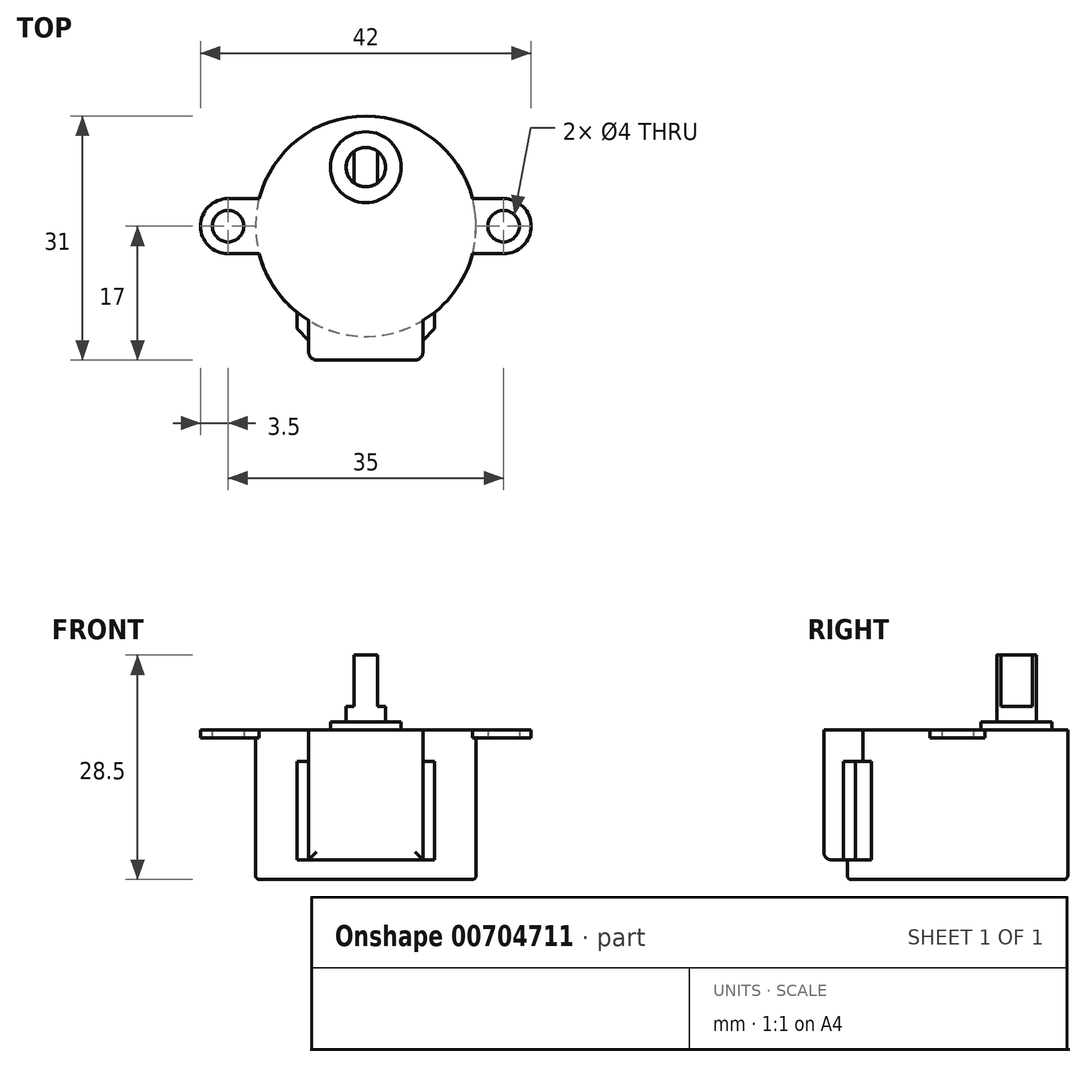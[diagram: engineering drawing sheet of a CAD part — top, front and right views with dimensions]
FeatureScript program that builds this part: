
annotation { "Feature Type Name" : "Feature", "Feature Type Description" : "" }
export const myFeature = defineFeature(function(context is Context, id is Id, definition is map)
    precondition{}
    {
        {
            var Q0;
            Q0=qCreatedBy(makeId("Top.planeOp"),FACE);
            var sketch = newSketch(context, id + "F0", { "sketchPlane" : qUnion([Q0])});
            skCircle(sketch, "E0", {"center": v(0, 0) * mm, "radius": 2.5 * mm});
            skLineSegment(sketch, "E1.bottom", {"start": v(-1.5, 2.88) * mm, "end": v(1.5, 2.88) * mm});
            skLineSegment(sketch, "E1.top", {"start": v(-1.5, -3.12) * mm, "end": v(1.5, -3.12) * mm});
            skLineSegment(sketch, "E1.left", {"start": v(-1.5, 2.88) * mm, "end": v(-1.5, -3.12) * mm});
            skLineSegment(sketch, "E1.right", {"start": v(1.5, 2.88) * mm, "end": v(1.5, -3.12) * mm});
            skCircle(sketch, "E2", {"center": v(0, 0) * mm, "radius": 4.5 * mm});
            skCircle(sketch, "E3", {"center": v(0, -7.5) * mm, "radius": 14 * mm});
            skCircle(sketch, "E4", {"center": v(17.5, -7.5) * mm, "radius": 2 * mm});
            skCircle(sketch, "E5", {"center": v(-17.5, -7.5) * mm, "radius": 2 * mm});
            skLineSegment(sketch, "E6", {"start": v(-37.47, -7.5) * mm, "end": v(35.56, -7.5) * mm, "construction": true});
            skCircle(sketch, "E7", {"center": v(17.5, -7.5) * mm, "radius": 3.5 * mm});
            skCircle(sketch, "E8", {"center": v(-17.5, -7.5) * mm, "radius": 3.5 * mm});
            skLineSegment(sketch, "E9", {"start": v(-17.5, -4) * mm, "end": v(17.5, -4) * mm});
            skLineSegment(sketch, "E10", {"start": v(-17.5, -11) * mm, "end": v(17.5, -11) * mm});
            skLineSegment(sketch, "E11.bottom", {"start": v(-7.25, -19.5) * mm, "end": v(7.25, -19.5) * mm});
            skLineSegment(sketch, "E11.top", {"start": v(-7.25, -24.5) * mm, "end": v(7.25, -24.5) * mm});
            skLineSegment(sketch, "E11.left", {"start": v(-7.25, -19.5) * mm, "end": v(-7.25, -24.5) * mm});
            skLineSegment(sketch, "E11.right", {"start": v(7.25, -19.5) * mm, "end": v(7.25, -24.5) * mm});
            skLineSegment(sketch, "E12.bottom", {"start": v(-8.75, -12.5) * mm, "end": v(8.75, -12.5) * mm});
            skLineSegment(sketch, "E12.top", {"start": v(-8.75, -20.5) * mm, "end": v(8.75, -20.5) * mm});
            skLineSegment(sketch, "E12.left", {"start": v(-8.75, -12.5) * mm, "end": v(-8.75, -20.5) * mm});
            skLineSegment(sketch, "E12.right", {"start": v(8.75, -12.5) * mm, "end": v(8.75, -20.5) * mm});
            skLineSegment(sketch, "E13", {"start": v(8.75, -20.5) * mm, "end": v(7.25, -22) * mm});
            skLineSegment(sketch, "E14", {"start": v(-8.75, -20.5) * mm, "end": v(-7.25, -22) * mm});
            skSolve(sketch);
        }
        {
            var Q0;
            {var subQ0=sQuery(id+"F0.wireOp",EDGE,"E9");var subQ9=sQuery(id+"F0.wireOp",EDGE,"E2");var subQ10=makeQuery(id+"F0.imprint","INTERSECT",VERTEX,{"disambiguationData":[OD(0.0)],"derivedFrom":[subQ9,subQ0]});Q0=makeQuery(id+"F0.imprint","IMPRINT",FACE,{"disambiguationData":[TD([[makeQuery(id+"F0.imprint","IMPRINT",EDGE,{"disambiguationData":[TD([[subQ10,-1.0]])],"derivedFrom":subQ9}),-1.0]])]});}
            var Q1;
            Q1=makeQuery(id+"F0.imprint","IMPRINT",FACE,{"disambiguationData":[TD([[makeQuery(id+"F0.imprint","IMPRINT",EDGE,{"derivedFrom":sQuery(id+"F0.wireOp",EDGE,"E4")}),-1.0]])]});
            var Q2;
            Q2=makeQuery(id+"F0.imprint","IMPRINT",FACE,{"disambiguationData":[TD([[makeQuery(id+"F0.imprint","IMPRINT",EDGE,{"derivedFrom":sQuery(id+"F0.wireOp",EDGE,"E5")}),-1.0]])]});
            var Q3;
            {var subQ0=sQuery(id+"F0.wireOp",EDGE,"E9");var subQ1=sQuery(id+"F0.wireOp",EDGE,"E3");var subQ2=makeQuery(id+"F0.imprint","INTERSECT",VERTEX,{"disambiguationData":[OD(1.0)],"derivedFrom":[subQ1,subQ0]});Q3=makeQuery(id+"F0.imprint","IMPRINT",FACE,{"disambiguationData":[TD([[makeQuery(id+"F0.imprint","IMPRINT",EDGE,{"disambiguationData":[TD([[subQ2,-1.0]])],"derivedFrom":subQ1}),-1.0]])]});}
            var Q4;
            {var subQ0=sQuery(id+"F0.wireOp",EDGE,"E10");var subQ1=sQuery(id+"F0.wireOp",EDGE,"E3");var subQ2=makeQuery(id+"F0.imprint","INTERSECT",VERTEX,{"disambiguationData":[OD(0.0)],"derivedFrom":[subQ1,subQ0]});Q4=makeQuery(id+"F0.imprint","IMPRINT",FACE,{"disambiguationData":[TD([[makeQuery(id+"F0.imprint","IMPRINT",EDGE,{"disambiguationData":[TD([[subQ2,1.0]])],"derivedFrom":subQ1}),-1.0]])]});}
            var Q5;
            {var subQ0=sQuery(id+"F0.wireOp",EDGE,"E12.bottom");Q5=makeQuery(id+"F0.imprint","IMPRINT",FACE,{"disambiguationData":[TD([[makeQuery(id+"F0.imprint","IMPRINT",EDGE,{"derivedFrom":subQ0}),1.0]])]});}
            var Q6;
            {var subQ0=sQuery(id+"F0.wireOp",EDGE,"E12.bottom");Q6=makeQuery(id+"F0.imprint","IMPRINT",FACE,{"disambiguationData":[TD([[makeQuery(id+"F0.imprint","IMPRINT",EDGE,{"derivedFrom":subQ0}),-1.0]])]});}
            var Q7;
            {var subQ0=sQuery(id+"F0.wireOp",EDGE,"E9");var subQ1=sQuery(id+"F0.wireOp",EDGE,"E2");var subQ2=makeQuery(id+"F0.imprint","INTERSECT",VERTEX,{"disambiguationData":[OD(0.0)],"derivedFrom":[subQ1,subQ0]});Q7=makeQuery(id+"F0.imprint","IMPRINT",FACE,{"disambiguationData":[TD([[makeQuery(id+"F0.imprint","IMPRINT",EDGE,{"disambiguationData":[TD([[subQ2,1.0]])],"derivedFrom":subQ1}),-1.0]])]});}
            var Q8;
            {var subQ0=sQuery(id+"F0.wireOp",EDGE,"E9");var subQ1=sQuery(id+"F0.wireOp",EDGE,"E3");var subQ2=makeQuery(id+"F0.imprint","INTERSECT",VERTEX,{"disambiguationData":[OD(0.0)],"derivedFrom":[subQ1,subQ0]});Q8=makeQuery(id+"F0.imprint","IMPRINT",FACE,{"disambiguationData":[TD([[makeQuery(id+"F0.imprint","IMPRINT",EDGE,{"disambiguationData":[TD([[subQ2,1.0]])],"derivedFrom":subQ1}),-1.0]])]});}
            var Q9;
            {var subQ0=sQuery(id+"F0.wireOp",EDGE,"E10");var subQ1=sQuery(id+"F0.wireOp",EDGE,"E3");var subQ2=makeQuery(id+"F0.imprint","INTERSECT",VERTEX,{"disambiguationData":[OD(1.0)],"derivedFrom":[subQ1,subQ0]});Q9=makeQuery(id+"F0.imprint","IMPRINT",FACE,{"disambiguationData":[TD([[makeQuery(id+"F0.imprint","IMPRINT",EDGE,{"disambiguationData":[TD([[subQ2,-1.0]])],"derivedFrom":subQ1}),-1.0]])]});}
            extrude(context, id + "F1", {"entities" : qUnion([Q0, Q1, Q2, Q3, Q4, Q5, Q6, Q7, Q8, Q9]), "depth" : 1 * mm});
        }
        {
            var Q0;
            {var subQ0=sQuery(id+"F0.wireOp",EDGE,"E9");var subQ1=sQuery(id+"F0.wireOp",EDGE,"E2");var subQ2=makeQuery(id+"F0.imprint","INTERSECT",VERTEX,{"disambiguationData":[OD(0.0)],"derivedFrom":[subQ1,subQ0]});Q0=makeQuery(id+"F0.imprint","IMPRINT",FACE,{"disambiguationData":[TD([[makeQuery(id+"F0.imprint","IMPRINT",EDGE,{"disambiguationData":[TD([[subQ2,1.0]])],"derivedFrom":subQ1}),-1.0]])]});}
            var Q1;
            {var subQ0=sQuery(id+"F0.wireOp",EDGE,"E9");var subQ9=sQuery(id+"F0.wireOp",EDGE,"E2");var subQ10=makeQuery(id+"F0.imprint","INTERSECT",VERTEX,{"disambiguationData":[OD(0.0)],"derivedFrom":[subQ9,subQ0]});Q1=makeQuery(id+"F0.imprint","IMPRINT",FACE,{"disambiguationData":[TD([[makeQuery(id+"F0.imprint","IMPRINT",EDGE,{"disambiguationData":[TD([[subQ10,-1.0]])],"derivedFrom":subQ9}),-1.0]])]});}
            var Q2;
            {var subQ0=sQuery(id+"F0.wireOp",EDGE,"E12.bottom");Q2=makeQuery(id+"F0.imprint","IMPRINT",FACE,{"disambiguationData":[TD([[makeQuery(id+"F0.imprint","IMPRINT",EDGE,{"derivedFrom":subQ0}),1.0]])]});}
            var Q3;
            {var subQ0=sQuery(id+"F0.wireOp",EDGE,"E12.bottom");Q3=makeQuery(id+"F0.imprint","IMPRINT",FACE,{"disambiguationData":[TD([[makeQuery(id+"F0.imprint","IMPRINT",EDGE,{"derivedFrom":subQ0}),-1.0]])]});}
            var Q4;
            {var subQ0=sQuery(id+"F0.wireOp",EDGE,"E12.top");var subQ1=sQuery(id+"F0.wireOp",EDGE,"E3");var subQ2=makeQuery(id+"F0.imprint","INTERSECT",VERTEX,{"disambiguationData":[OD(0.0)],"derivedFrom":[subQ1,subQ0]});Q4=makeQuery(id+"F0.imprint","IMPRINT",FACE,{"disambiguationData":[TD([[makeQuery(id+"F0.imprint","IMPRINT",EDGE,{"disambiguationData":[TD([[subQ2,-1.0]])],"derivedFrom":subQ1}),1.0]])]});}
            var Q5;
            {var subQ0=sQuery(id+"F0.wireOp",EDGE,"E11.bottom");var subQ1=sQuery(id+"F0.wireOp",EDGE,"E3");var subQ2=makeQuery(id+"F0.imprint","INTERSECT",VERTEX,{"disambiguationData":[OD(0.0)],"derivedFrom":[subQ1,subQ0]});Q5=makeQuery(id+"F0.imprint","IMPRINT",FACE,{"disambiguationData":[TD([[makeQuery(id+"F0.imprint","IMPRINT",EDGE,{"disambiguationData":[TD([[subQ2,-1.0]])],"derivedFrom":subQ1}),1.0]])]});}
            var Q6;
            {var subQ1=sQuery(id+"F0.wireOp",EDGE,"E1.bottom");Q6=makeQuery(id+"F0.imprint","IMPRINT",FACE,{"disambiguationData":[TD([[makeQuery(id+"F0.imprint","IMPRINT",EDGE,{"derivedFrom":subQ1}),1.0]])]});}
            var Q7;
            {var subQ0=sQuery(id+"F0.wireOp",EDGE,"E9");var subQ1=sQuery(id+"F0.wireOp",EDGE,"E2");var subQ2=makeQuery(id+"F0.imprint","INTERSECT",VERTEX,{"disambiguationData":[OD(0.0)],"derivedFrom":[subQ1,subQ0]});Q7=makeQuery(id+"F0.imprint","IMPRINT",FACE,{"disambiguationData":[TD([[makeQuery(id+"F0.imprint","IMPRINT",EDGE,{"disambiguationData":[TD([[subQ2,-1.0]])],"derivedFrom":subQ1}),1.0]])]});}
            var Q8;
            {var subQ5=sQuery(id+"F0.wireOp",EDGE,"E1.bottom");Q8=makeQuery(id+"F0.imprint","IMPRINT",FACE,{"disambiguationData":[TD([[makeQuery(id+"F0.imprint","IMPRINT",EDGE,{"derivedFrom":subQ5}),-1.0]])]});}
            var Q9;
            {var subQ0=sQuery(id+"F0.wireOp",EDGE,"E1.left");var subQ1=sQuery(id+"F0.wireOp",EDGE,"E0");var subQ2=makeQuery(id+"F0.imprint","INTERSECT",VERTEX,{"disambiguationData":[OD(0.0)],"derivedFrom":[subQ1,subQ0]});Q9=makeQuery(id+"F0.imprint","IMPRINT",FACE,{"disambiguationData":[TD([[makeQuery(id+"F0.imprint","IMPRINT",EDGE,{"disambiguationData":[TD([[subQ2,1.0]])],"derivedFrom":subQ1}),1.0]])]});}
            var Q10;
            {var subQ0=sQuery(id+"F0.wireOp",EDGE,"E1.right");var subQ1=sQuery(id+"F0.wireOp",EDGE,"E0");var subQ2=makeQuery(id+"F0.imprint","INTERSECT",VERTEX,{"disambiguationData":[OD(0.0)],"derivedFrom":[subQ1,subQ0]});Q10=makeQuery(id+"F0.imprint","IMPRINT",FACE,{"disambiguationData":[TD([[makeQuery(id+"F0.imprint","IMPRINT",EDGE,{"disambiguationData":[TD([[subQ2,1.0]])],"derivedFrom":subQ1}),1.0]])]});}
            var Q11;
            {var subQ5=sQuery(id+"F0.wireOp",EDGE,"E1.top");Q11=makeQuery(id+"F0.imprint","IMPRINT",FACE,{"disambiguationData":[TD([[makeQuery(id+"F0.imprint","IMPRINT",EDGE,{"derivedFrom":subQ5}),1.0]])]});}
            var Q12;
            {var subQ0=sQuery(id+"F0.wireOp",EDGE,"E1.left");var subQ1=sQuery(id+"F0.wireOp",EDGE,"E0");var subQ2=makeQuery(id+"F0.imprint","INTERSECT",VERTEX,{"disambiguationData":[OD(0.0)],"derivedFrom":[subQ1,subQ0]});Q12=makeQuery(id+"F0.imprint","IMPRINT",FACE,{"disambiguationData":[TD([[makeQuery(id+"F0.imprint","IMPRINT",EDGE,{"disambiguationData":[TD([[subQ2,-1.0]])],"derivedFrom":subQ1}),1.0]])]});}
            extrude(context, id + "F2", {"entities" : qUnion([Q0, Q1, Q2, Q3, Q4, Q5, Q6, Q7, Q8, Q9, Q10, Q11, Q12]), "operationType" : NewBodyOperationType.ADD, "oppositeDirection" : true, "depth" : 18 * mm});
        }
        {
            var Q0;
            {var subQ1=sQuery(id+"F0.wireOp",EDGE,"E11.top");Q0=makeQuery(id+"F0.imprint","IMPRINT",FACE,{"disambiguationData":[TD([[makeQuery(id+"F0.imprint","IMPRINT",EDGE,{"derivedFrom":subQ1}),1.0]])]});}
            var Q1;
            {var subQ0=sQuery(id+"F0.wireOp",EDGE,"E11.bottom");var subQ1=sQuery(id+"F0.wireOp",EDGE,"E3");var subQ2=makeQuery(id+"F0.imprint","INTERSECT",VERTEX,{"disambiguationData":[OD(0.0)],"derivedFrom":[subQ1,subQ0]});Q1=makeQuery(id+"F0.imprint","IMPRINT",FACE,{"disambiguationData":[TD([[makeQuery(id+"F0.imprint","IMPRINT",EDGE,{"disambiguationData":[TD([[subQ2,-1.0]])],"derivedFrom":subQ1}),-1.0]])]});}
            var Q2;
            {var subQ0=sQuery(id+"F0.wireOp",EDGE,"E12.top");var subQ1=sQuery(id+"F0.wireOp",EDGE,"E3");var subQ2=makeQuery(id+"F0.imprint","INTERSECT",VERTEX,{"disambiguationData":[OD(0.0)],"derivedFrom":[subQ1,subQ0]});Q2=makeQuery(id+"F0.imprint","IMPRINT",FACE,{"disambiguationData":[TD([[makeQuery(id+"F0.imprint","IMPRINT",EDGE,{"disambiguationData":[TD([[subQ2,-1.0]])],"derivedFrom":subQ1}),1.0]])]});}
            var Q3;
            {var subQ0=sQuery(id+"F0.wireOp",EDGE,"E11.bottom");var subQ1=sQuery(id+"F0.wireOp",EDGE,"E3");var subQ2=makeQuery(id+"F0.imprint","INTERSECT",VERTEX,{"disambiguationData":[OD(0.0)],"derivedFrom":[subQ1,subQ0]});Q3=makeQuery(id+"F0.imprint","IMPRINT",FACE,{"disambiguationData":[TD([[makeQuery(id+"F0.imprint","IMPRINT",EDGE,{"disambiguationData":[TD([[subQ2,-1.0]])],"derivedFrom":subQ1}),1.0]])]});}
            var Q4;
            {var subQ0=sQuery(id+"F0.wireOp",EDGE,"E12.top");var subQ1=sQuery(id+"F0.wireOp",EDGE,"E3");var subQ2=makeQuery(id+"F0.imprint","INTERSECT",VERTEX,{"disambiguationData":[OD(1.0)],"derivedFrom":[subQ1,subQ0]});Q4=makeQuery(id+"F0.imprint","IMPRINT",FACE,{"disambiguationData":[TD([[makeQuery(id+"F0.imprint","IMPRINT",EDGE,{"disambiguationData":[TD([[subQ2,-1.0]])],"derivedFrom":subQ1}),-1.0]])]});}
            extrude(context, id + "F3", {"entities" : qUnion([Q0, Q1, Q2, Q3, Q4]), "operationType" : NewBodyOperationType.ADD, "oppositeDirection" : true, "depth" : 15.5 * mm, "hasSecondDirection" : true, "secondDirectionOppositeDirection" : false, "secondDirectionDepth" : 1 * mm});
        }
        {
            var Q0;
            {var subQ0=sQuery(id+"F0.wireOp",EDGE,"E12.right");var subQ7=sQuery(id+"F0.wireOp",EDGE,"E3");var subQ9=makeQuery(id+"F0.imprint","INTERSECT",VERTEX,{"derivedFrom":[subQ7,subQ0]});Q0=makeQuery(id+"F0.imprint","IMPRINT",FACE,{"disambiguationData":[TD([[makeQuery(id+"F0.imprint","IMPRINT",EDGE,{"disambiguationData":[TD([[subQ9,1.0]])],"derivedFrom":subQ7}),-1.0]])]});}
            var Q1;
            {var subQ0=sQuery(id+"F0.wireOp",EDGE,"E13");Q1=makeQuery(id+"F0.imprint","IMPRINT",FACE,{"disambiguationData":[TD([[makeQuery(id+"F0.imprint","IMPRINT",EDGE,{"derivedFrom":subQ0}),-1.0]])]});}
            var Q2;
            {var subQ0=sQuery(id+"F0.wireOp",EDGE,"E12.left");var subQ7=sQuery(id+"F0.wireOp",EDGE,"E3");var subQ9=makeQuery(id+"F0.imprint","INTERSECT",VERTEX,{"derivedFrom":[subQ7,subQ0]});Q2=makeQuery(id+"F0.imprint","IMPRINT",FACE,{"disambiguationData":[TD([[makeQuery(id+"F0.imprint","IMPRINT",EDGE,{"disambiguationData":[TD([[subQ9,-1.0]])],"derivedFrom":subQ7}),-1.0]])]});}
            var Q3;
            {var subQ0=sQuery(id+"F0.wireOp",EDGE,"E14");Q3=makeQuery(id+"F0.imprint","IMPRINT",FACE,{"disambiguationData":[TD([[makeQuery(id+"F0.imprint","IMPRINT",EDGE,{"derivedFrom":subQ0}),1.0]])]});}
            extrude(context, id + "F4", {"entities" : qUnion([Q0, Q1, Q2, Q3]), "operationType" : NewBodyOperationType.ADD, "oppositeDirection" : true, "depth" : 15.5 * mm, "hasSecondDirection" : true, "secondDirectionOppositeDirection" : true, "secondDirectionDepth" : 3 * mm});
        }
        {
            var Q0;
            {var subQ1=sQuery(id+"F0.wireOp",EDGE,"E1.bottom");Q0=makeQuery(id+"F0.imprint","IMPRINT",FACE,{"disambiguationData":[TD([[makeQuery(id+"F0.imprint","IMPRINT",EDGE,{"derivedFrom":subQ1}),1.0]])]});}
            var Q1;
            {var subQ5=sQuery(id+"F0.wireOp",EDGE,"E1.bottom");Q1=makeQuery(id+"F0.imprint","IMPRINT",FACE,{"disambiguationData":[TD([[makeQuery(id+"F0.imprint","IMPRINT",EDGE,{"derivedFrom":subQ5}),-1.0]])]});}
            var Q2;
            {var subQ5=sQuery(id+"F0.wireOp",EDGE,"E1.top");Q2=makeQuery(id+"F0.imprint","IMPRINT",FACE,{"disambiguationData":[TD([[makeQuery(id+"F0.imprint","IMPRINT",EDGE,{"derivedFrom":subQ5}),1.0]])]});}
            var Q3;
            {var subQ0=sQuery(id+"F0.wireOp",EDGE,"E9");var subQ1=sQuery(id+"F0.wireOp",EDGE,"E2");var subQ2=makeQuery(id+"F0.imprint","INTERSECT",VERTEX,{"disambiguationData":[OD(0.0)],"derivedFrom":[subQ1,subQ0]});Q3=makeQuery(id+"F0.imprint","IMPRINT",FACE,{"disambiguationData":[TD([[makeQuery(id+"F0.imprint","IMPRINT",EDGE,{"disambiguationData":[TD([[subQ2,-1.0]])],"derivedFrom":subQ1}),1.0]])]});}
            extrude(context, id + "F5", {"entities" : qUnion([Q0, Q1, Q2, Q3]), "operationType" : NewBodyOperationType.ADD, "depth" : 2 * mm});
        }
        {
            var Q0;
            {var subQ0=sQuery(id+"F0.wireOp",EDGE,"E1.right");var subQ1=sQuery(id+"F0.wireOp",EDGE,"E0");var subQ2=makeQuery(id+"F0.imprint","INTERSECT",VERTEX,{"disambiguationData":[OD(0.0)],"derivedFrom":[subQ1,subQ0]});Q0=makeQuery(id+"F0.imprint","IMPRINT",FACE,{"disambiguationData":[TD([[makeQuery(id+"F0.imprint","IMPRINT",EDGE,{"disambiguationData":[TD([[subQ2,1.0]])],"derivedFrom":subQ1}),1.0]])]});}
            var Q1;
            {var subQ0=sQuery(id+"F0.wireOp",EDGE,"E1.left");var subQ1=sQuery(id+"F0.wireOp",EDGE,"E0");var subQ2=makeQuery(id+"F0.imprint","INTERSECT",VERTEX,{"disambiguationData":[OD(0.0)],"derivedFrom":[subQ1,subQ0]});Q1=makeQuery(id+"F0.imprint","IMPRINT",FACE,{"disambiguationData":[TD([[makeQuery(id+"F0.imprint","IMPRINT",EDGE,{"disambiguationData":[TD([[subQ2,1.0]])],"derivedFrom":subQ1}),1.0]])]});}
            var Q2;
            {var subQ0=sQuery(id+"F0.wireOp",EDGE,"E1.left");var subQ1=sQuery(id+"F0.wireOp",EDGE,"E0");var subQ2=makeQuery(id+"F0.imprint","INTERSECT",VERTEX,{"disambiguationData":[OD(0.0)],"derivedFrom":[subQ1,subQ0]});Q2=makeQuery(id+"F0.imprint","IMPRINT",FACE,{"disambiguationData":[TD([[makeQuery(id+"F0.imprint","IMPRINT",EDGE,{"disambiguationData":[TD([[subQ2,-1.0]])],"derivedFrom":subQ1}),1.0]])]});}
            extrude(context, id + "F6", {"entities" : qUnion([Q0, Q1, Q2]), "operationType" : NewBodyOperationType.ADD, "depth" : 4 * mm});
        }
        {
            var Q0;
            {var subQ0=sQuery(id+"F0.wireOp",EDGE,"E1.left");var subQ1=sQuery(id+"F0.wireOp",EDGE,"E0");var subQ2=makeQuery(id+"F0.imprint","INTERSECT",VERTEX,{"disambiguationData":[OD(0.0)],"derivedFrom":[subQ1,subQ0]});Q0=makeQuery(id+"F0.imprint","IMPRINT",FACE,{"disambiguationData":[TD([[makeQuery(id+"F0.imprint","IMPRINT",EDGE,{"disambiguationData":[TD([[subQ2,1.0]])],"derivedFrom":subQ1}),1.0]])]});}
            extrude(context, id + "F7", {"entities" : qUnion([Q0]), "operationType" : NewBodyOperationType.ADD, "depth" : 10.5 * mm});
        }
        {
            var Q0;
            Q0=makeQuery(id+"F2.opExtrude","CAP_FACE",FACE,{"disambiguationData":[OSD([sQuery(id+"F0.wireOp",EDGE,"E3")])],"isStart":false});
            fillet(context, id + "F8", {"entities" : qUnion([Q0]), "radius" : 0.5 * mm, "tangentPropagation" : true, "allowEdgeOverflow" : false});
        }
        {
            var Q0;
            Q0=makeQuery(id+"F3.opExtrude","SWEPT_EDGE",EDGE,{"disambiguationData":[OSD([sQuery(id+"F0.wireOp",EDGE,"E11.top"),sQuery(id+"F0.wireOp",EDGE,"E11.left")])]});
            var Q1;
            Q1=makeQuery(id+"F3.opExtrude","CAP_EDGE",EDGE,{"disambiguationData":[OSD([sQuery(id+"F0.wireOp",EDGE,"E11.top")])],"isStart":false});
            var Q2;
            Q2=makeQuery(id+"F3.opExtrude","SWEPT_EDGE",EDGE,{"disambiguationData":[OSD([sQuery(id+"F0.wireOp",EDGE,"E11.top"),sQuery(id+"F0.wireOp",EDGE,"E11.right")])]});
            fillet(context, id + "F9", {"entities" : qUnion([Q0, Q1, Q2]), "radius" : 1 * mm, "tangentPropagation" : true, "allowEdgeOverflow" : false});
        }
    });
